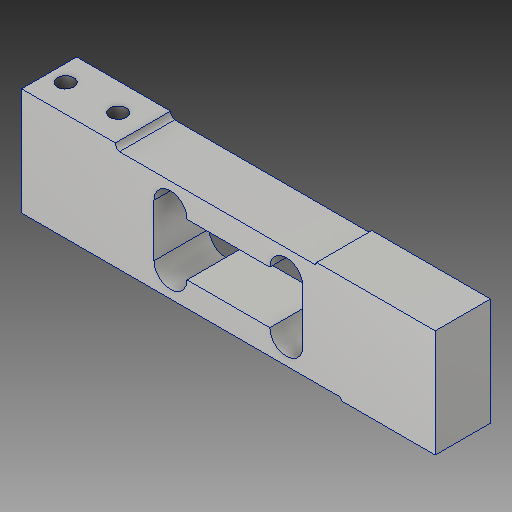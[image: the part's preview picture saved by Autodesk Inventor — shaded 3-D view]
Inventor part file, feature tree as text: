
AUTODESK INVENTOR PART (.ipt)
format: ipt  version: 2018.1 (Build 221171000, 171)  size: 187,904 bytes
history: native  units: mm
features: thread x4, extrude x3, sketch x3, other x1
ambient origin geometry x8: Origin, YZ Plane, XZ Plane, XY Plane, X Axis, Y Axis, Z Axis, Center Point
bodies: Solid1 (feature_tree)
feature tree (11):
  parser-record x1  (decoder bookkeeping rows leaked as tree rows — omitted from the tree; the rows remain in map.json)
  extrude  "Extrusion1"  Depth=39.0mm
  extrude  "Extrusion4"  Depth=1.0mm
  extrude  "Extrusion5"  Depth=10.0mm
  thread  "Thread1"  [1 undecoded]
  thread  "Thread2"  [1 undecoded]
  thread  "Thread3"  [1 undecoded]
  thread  "Thread4"  [1 undecoded]
  sketch  "Sketch1"  dims[d0=150.0mm d1=39.0mm]
  sketch  "Sketch2"  dims[d9=34.0mm d11=1.0mm]
  sketch  "Sketch3"  dims[d17=1.0mm d18=43.0mm d19=1.25mm d20=1.0mm d21=2.5mm d22=2.0mm d23=1.0mm d24=34.0mm d25=1.25mm d26=1.0mm d27=15.0mm d29=12.0mm d30=6.0mm d31=20.0mm d32=0.0mm d33=6.0mm d34=10.0mm d35=25.0mm d36=6.0mm d37=19.05mm d43=18.0mm d44=0.0mm d45=6.0mm d46=6.0mm d47=19.05mm d48=6.0mm d49=19.05mm d51=125.0mm d52=10.0mm d53=10.0mm d54=18.0mm d55=0.0mm d56=10.0mm d57=0.0mm d58=10.0mm d59=0.0mm d60=10.0mm d61=0.0mm d62=10.0mm d63=0.0mm]
note: 4 required parameter values undecoded (feature->parameter linkage not recoverable at this tier; creation-order binding heuristic only, values carry confidence <= 0.55)
note: 1 file-system path scrubbed to <path> (originals preserved in map.json)
